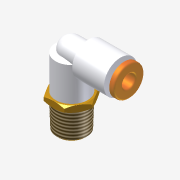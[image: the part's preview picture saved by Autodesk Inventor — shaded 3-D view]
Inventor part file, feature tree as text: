
AUTODESK INVENTOR PART (.ipt)
format: ipt  version: 2014 SP1 (Build 180222100, 222)  size: 184,832 bytes
history: native  units: mm
features: imported_body x1, thread x1
ambient origin geometry x8: Origin, YZ Plane, XZ Plane, XY Plane, X Axis, Y Axis, Z Axis, Center Point
bodies: Solid1 (feature_tree)
feature tree (2):
  imported_body  "Base1"
  thread  "Thread1"  [1 undecoded]
note: 1 required parameter value undecoded (feature->parameter linkage not recoverable at this tier; creation-order binding heuristic only, values carry confidence <= 0.55)
